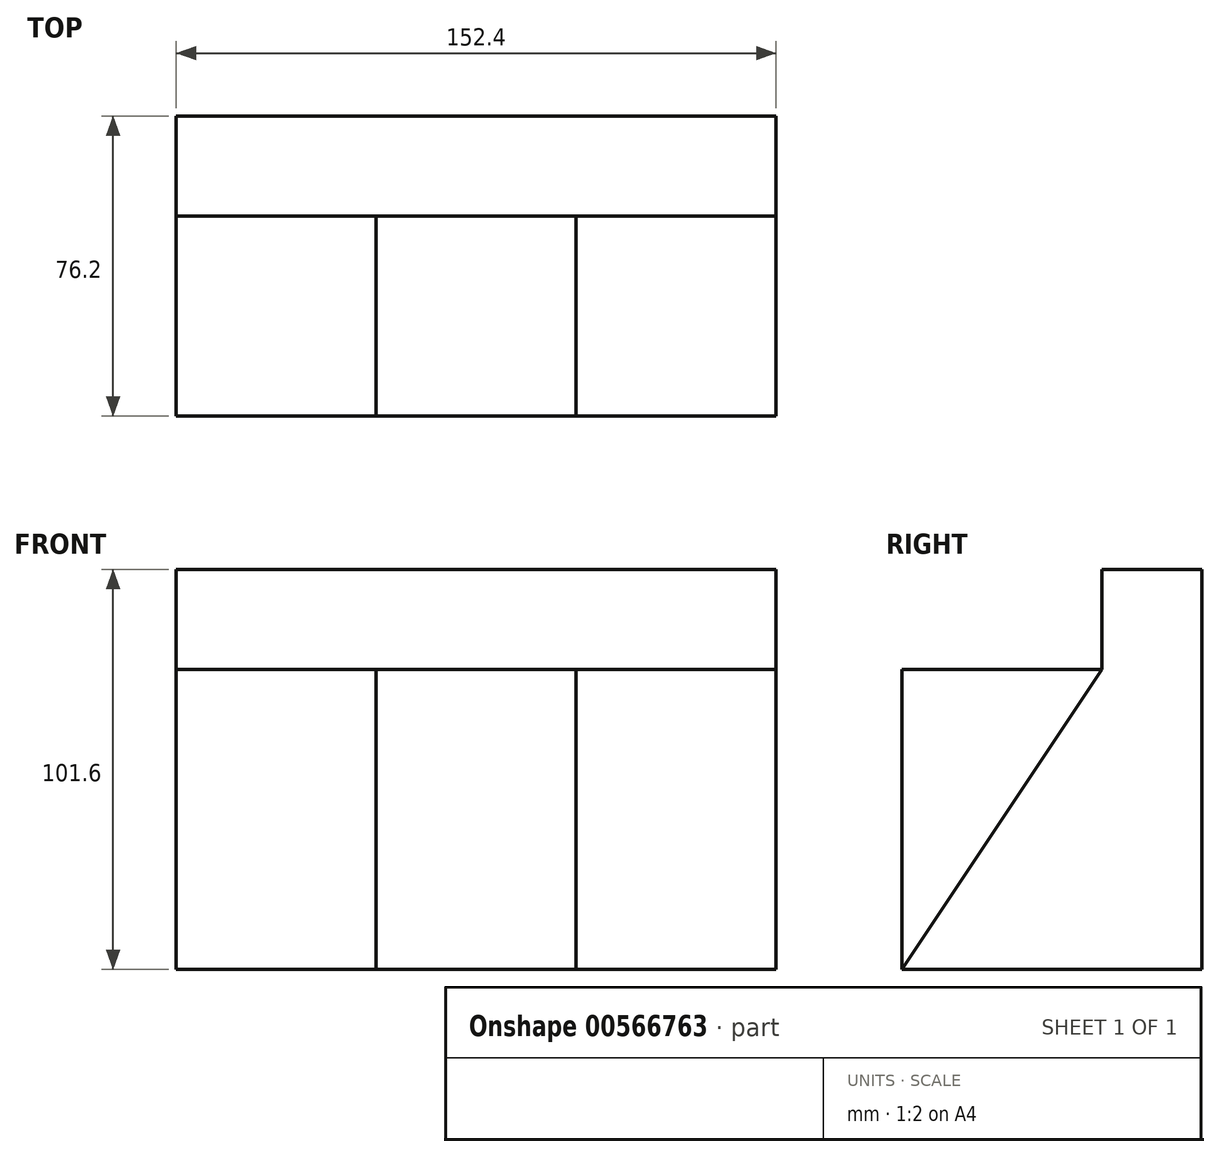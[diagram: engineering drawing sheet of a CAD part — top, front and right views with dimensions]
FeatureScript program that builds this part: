
annotation { "Feature Type Name" : "Feature", "Feature Type Description" : "" }
export const myFeature = defineFeature(function(context is Context, id is Id, definition is map)
    precondition{}
    {
        {
            var Q0;
            Q0=qCreatedBy(makeId("Top.planeOp"),FACE);
            var sketch = newSketch(context, id + "F0", { "sketchPlane" : qUnion([Q0])});
            skLineSegment(sketch, "E0.bottom", {"start": v(-69.4, 16.66) * mm, "end": v(83, 16.66) * mm});
            skLineSegment(sketch, "E0.top", {"start": v(-69.4, -59.54) * mm, "end": v(83, -59.54) * mm});
            skLineSegment(sketch, "E0.left", {"start": v(-69.4, 16.66) * mm, "end": v(-69.4, -59.54) * mm});
            skLineSegment(sketch, "E0.right", {"start": v(83, 16.66) * mm, "end": v(83, -59.54) * mm});
            skSolve(sketch);
        }
        {
            var Q0;
            Q0=makeQuery(id+"F0.imprint","IMPRINT",FACE,{"disambiguationData":[TD([[makeQuery(id+"F0.imprint","IMPRINT",EDGE,{"derivedFrom":sQuery(id+"F0.wireOp",EDGE,"E0.bottom")}),-1.0]])]});
            extrude(context, id + "F1", {"entities" : qUnion([Q0]), "depth" : 101.6 * mm, "offsetDistance" : 25.4 * mm});
        }
        {
            var Q0;
            Q0=makeQuery(id+"F1.opExtrude","SWEPT_FACE",FACE,{"disambiguationData":[OSD([sQuery(id+"F0.wireOp",EDGE,"E0.right")])]});
            var sketch = newSketch(context, id + "F2", { "sketchPlane" : qUnion([Q0])});
            skLineSegment(sketch, "E1.right", {"start": v(16.66, 76.2) * mm, "end": v(16.66, 0) * mm});
            skLineSegment(sketch, "E2.bottom", {"start": v(16.66, 76.2) * mm, "end": v(-8.74, 76.2) * mm});
            skLineSegment(sketch, "E2.top", {"start": v(16.66, 0) * mm, "end": v(-8.74, 0) * mm});
            skLineSegment(sketch, "E2.right", {"start": v(-8.74, 76.2) * mm, "end": v(-8.74, 0) * mm});
            skLineSegment(sketch, "E3", {"start": v(-8.74, 76.2) * mm, "end": v(-59.54, 0) * mm});
            skLineSegment(sketch, "E4.bottom", {"start": v(-8.74, 76.2) * mm, "end": v(16.66, 76.2) * mm});
            skLineSegment(sketch, "E4.top", {"start": v(-8.74, 101.6) * mm, "end": v(16.66, 101.6) * mm});
            skLineSegment(sketch, "E4.left", {"start": v(-8.74, 76.2) * mm, "end": v(-8.74, 101.6) * mm});
            skLineSegment(sketch, "E4.right", {"start": v(16.66, 76.2) * mm, "end": v(16.66, 101.6) * mm});
            skSolve(sketch);
        }
        {
            var Q0;
            Q0=makeQuery(id+"F1.opExtrude","SWEPT_FACE",FACE,{"disambiguationData":[OSD([sQuery(id+"F0.wireOp",EDGE,"E0.top")])]});
            var sketch = newSketch(context, id + "F3", { "sketchPlane" : qUnion([Q0])});
            skLineSegment(sketch, "E5.bottom", {"start": v(-69.4, 76.2) * mm, "end": v(-18.6, 76.2) * mm});
            skLineSegment(sketch, "E5.top", {"start": v(-69.4, 0) * mm, "end": v(-18.6, 0) * mm});
            skLineSegment(sketch, "E5.left", {"start": v(-69.4, 76.2) * mm, "end": v(-69.4, 0) * mm});
            skLineSegment(sketch, "E5.right", {"start": v(-18.6, 76.2) * mm, "end": v(-18.6, 0) * mm});
            skLineSegment(sketch, "E6.bottom", {"start": v(-18.6, 76.2) * mm, "end": v(32.2, 76.2) * mm});
            skLineSegment(sketch, "E6.top", {"start": v(-18.6, 0) * mm, "end": v(32.2, 0) * mm});
            skLineSegment(sketch, "E6.right", {"start": v(32.2, 76.2) * mm, "end": v(32.2, 0) * mm});
            skLineSegment(sketch, "E7.bottom", {"start": v(32.2, 76.2) * mm, "end": v(83, 76.2) * mm});
            skLineSegment(sketch, "E7.top", {"start": v(32.2, 0) * mm, "end": v(83, 0) * mm});
            skLineSegment(sketch, "E7.right", {"start": v(83, 76.2) * mm, "end": v(83, 0) * mm});
            skSolve(sketch);
        }
        {
            var Q0;
            {var subQ4=sQuery(id+"F3.wireOp",EDGE,"E5.bottom");Q0=makeQuery(id+"F3.imprint","IMPRINT",FACE,{"disambiguationData":[TD([[makeQuery(id+"F3.imprint","IMPRINT",EDGE,{"derivedFrom":subQ4}),1.0]])]});}
            extrude(context, id + "F4", {"entities" : qUnion([Q0]), "operationType" : NewBodyOperationType.REMOVE, "oppositeDirection" : true, "depth" : 50.8 * mm, "offsetDistance" : 25.4 * mm});
        }
        {
            var Q0;
            Q0=makeQuery(id+"F2.imprint","IMPRINT",FACE,{"disambiguationData":[TD([[makeQuery(id+"F2.imprint","IMPRINT",EDGE,{"derivedFrom":sQuery(id+"F2.wireOp",EDGE,"E3")}),-1.0]])]});
            extrude(context, id + "F5", {"entities" : qUnion([Q0]), "operationType" : NewBodyOperationType.REMOVE, "oppositeDirection" : true, "depth" : 50.8 * mm, "offsetDistance" : 25.4 * mm});
        }
        {
            var Q0;
            Q0=makeQuery(id+"F1.opExtrude","SWEPT_FACE",FACE,{"disambiguationData":[OSD([sQuery(id+"F0.wireOp",EDGE,"E0.left")])]});
            var sketch = newSketch(context, id + "F6", { "sketchPlane" : qUnion([Q0])});
            skLineSegment(sketch, "E8", {"start": v(8.74, 76.2) * mm, "end": v(59.54, 0) * mm});
            skSolve(sketch);
        }
        {
            var Q0;
            Q0 = qSketchRegion(id + "F6", true);
            var Q1;
            Q1=makeQuery(id+"F6.imprint","IMPRINT",FACE,{"disambiguationData":[TD([[makeQuery(id+"F6.imprint","IMPRINT",EDGE,{"derivedFrom":sQuery(id+"F6.wireOp",EDGE,"E8")}),1.0]])]});
            extrude(context, id + "F7", {"entities" : qUnion([Q0, Q1]), "operationType" : NewBodyOperationType.REMOVE, "oppositeDirection" : true, "depth" : 50.8 * mm, "offsetDistance" : 25.4 * mm});
        }
    });
